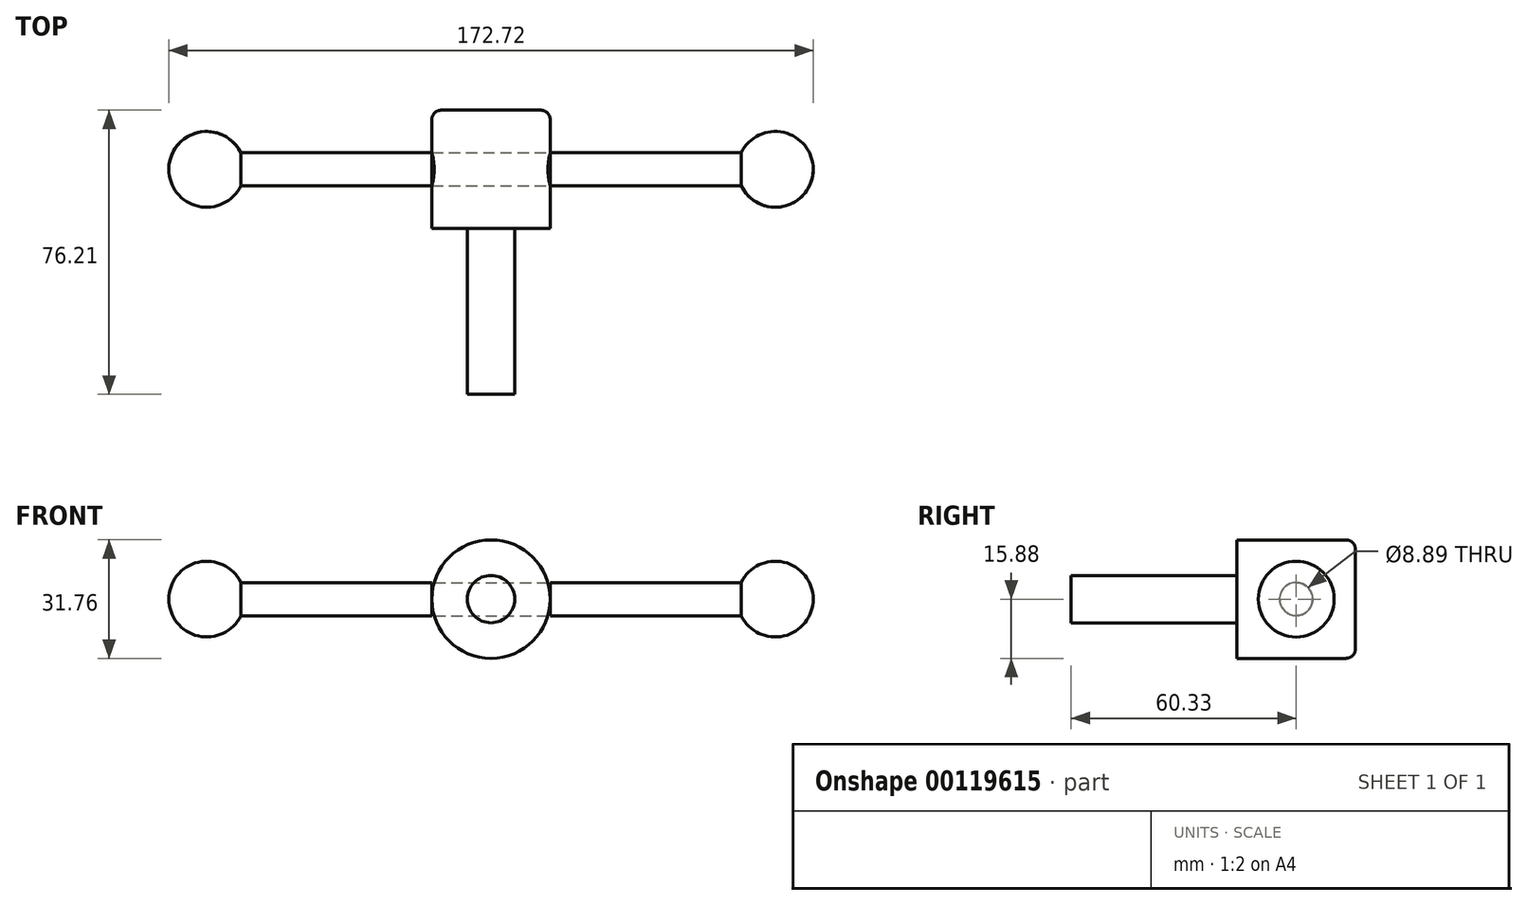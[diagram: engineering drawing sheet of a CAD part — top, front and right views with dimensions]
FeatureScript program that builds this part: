
annotation { "Feature Type Name" : "Feature", "Feature Type Description" : "" }
export const myFeature = defineFeature(function(context is Context, id is Id, definition is map)
    precondition{}
    {
        {
            var Q0;
            Q0=qCreatedBy(makeId("Top.planeOp"),FACE);
            var sketch = newSketch(context, id + "F0", { "sketchPlane" : qUnion([Q0])});
            skLineSegment(sketch, "E0", {"start": v(-76.2, 0) * mm, "end": v(76.2, 0) * mm, "construction": true});
            skLineSegment(sketch, "E1", {"start": v(0, 22.54) * mm, "end": v(0, -99.25) * mm, "construction": true});
            skLineSegment(sketch, "E2.bottom", {"start": v(-66.04, 0) * mm, "end": v(-15.87, 0) * mm});
            skLineSegment(sketch, "E2.top", {"start": v(-67.06, -4.45) * mm, "end": v(-15.87, -4.45) * mm});
            skLineSegment(sketch, "E2.right", {"start": v(-15.87, 0) * mm, "end": v(-15.87, -4.45) * mm});
            skLineSegment(sketch, "E3.bottom", {"start": v(-15.87, 15.87) * mm, "end": v(15.88, 15.87) * mm, "construction": true});
            skLineSegment(sketch, "E3.top", {"start": v(-15.87, -15.88) * mm, "end": v(15.88, -15.88) * mm, "construction": true});
            skLineSegment(sketch, "E3.left", {"start": v(-15.87, 15.87) * mm, "end": v(-15.87, -15.88) * mm});
            skLineSegment(sketch, "E3.right", {"start": v(15.88, 15.87) * mm, "end": v(15.88, -15.88) * mm, "construction": true});
            skLineSegment(sketch, "E4.bottom", {"start": v(66.04, 0) * mm, "end": v(15.88, 0) * mm});
            skLineSegment(sketch, "E4.top", {"start": v(67.06, -4.45) * mm, "end": v(15.88, -4.45) * mm});
            skLineSegment(sketch, "E4.right", {"start": v(15.88, 0) * mm, "end": v(15.88, -4.45) * mm});
            skArc(sketch, "E5", {"start": v(67.06, -4.44) * mm, "mid": v(78.48, -9.9) * mm, "end": v(86.36, 0) * mm});
            skArc(sketch, "E6", {"start": v(-86.36, 0) * mm, "mid": v(-78.48, -9.9) * mm, "end": v(-67.06, -4.45) * mm});
            skLineSegment(sketch, "E7.bottom", {"start": v(-6.35, -15.88) * mm, "end": v(0, -15.88) * mm});
            skLineSegment(sketch, "E7.top", {"start": v(-6.35, -60.33) * mm, "end": v(0, -60.33) * mm});
            skLineSegment(sketch, "E7.left", {"start": v(-6.35, -15.88) * mm, "end": v(-6.35, -60.33) * mm});
            skLineSegment(sketch, "E7.right", {"start": v(0, -15.88) * mm, "end": v(0, -60.33) * mm});
            skLineSegment(sketch, "E8", {"start": v(-66.04, 0) * mm, "end": v(-86.36, 0) * mm});
            skLineSegment(sketch, "E9", {"start": v(66.04, 0) * mm, "end": v(86.36, 0) * mm});
            skLineSegment(sketch, "E10", {"start": v(0, 15.87) * mm, "end": v(0, -15.88) * mm});
            skLineSegment(sketch, "E11", {"start": v(0, 15.87) * mm, "end": v(-15.87, 15.87) * mm});
            skLineSegment(sketch, "E12", {"start": v(0, -15.88) * mm, "end": v(-15.87, -15.88) * mm});
            skLineSegment(sketch, "E13", {"start": v(-15.87, 0) * mm, "end": v(15.88, 0) * mm});
            skLineSegment(sketch, "E14", {"start": v(-15.87, -4.45) * mm, "end": v(15.88, -4.44) * mm});
            skSolve(sketch);
        }
        {
            var Q0;
            {var subQ0=sQuery(id+"F0.wireOp",EDGE,"E10");Q0=makeQuery(id+"F0.imprint","IMPRINT",FACE,{"disambiguationData":[TD([[makeQuery(id+"F0.imprint","IMPRINT",EDGE,{"derivedFrom":subQ0}),-1.0]])]});}
            var Q1;
            Q1=makeQuery(id+"F0.imprint","IMPRINT",FACE,{"disambiguationData":[TD([[makeQuery(id+"F0.imprint","IMPRINT",EDGE,{"derivedFrom":sQuery(id+"F0.wireOp",EDGE,"E7.top")}),1.0]])]});
            var Q2;
            {var subQ0=sQuery(id+"F0.wireOp",EDGE,"E12");var subQ5=sQuery(id+"F0.wireOp",EDGE,"E3.left");var subQ6=makeQuery(id+"F0.imprint","INTERSECT",VERTEX,{"derivedFrom":[subQ5,subQ0]});Q2=makeQuery(id+"F0.imprint","IMPRINT",FACE,{"disambiguationData":[TD([[makeQuery(id+"F0.imprint","IMPRINT",EDGE,{"disambiguationData":[TD([[subQ6,1.0]])],"derivedFrom":subQ0}),-1.0]])]});}
            var Q3;
            Q3=sQuery(id+"F0.wireOp",EDGE,"E1");
            revolve(context, id + "F1", {"entities" : qUnion([Q0, Q1, Q2]), "axis" : qUnion([Q3]), "revolveType" : RevolveType.FULL});
        }
        {
            var Q0;
            Q0=qCreatedBy(makeId("Right.planeOp"),FACE);
            cPlane(context, id + "F2", {"entities" : qUnion([Q0]), "cplaneType" : CPlaneType.OFFSET, "offset" : 15.88 * mm, "width" : 152.4 * mm, "height" : 152.4 * mm});
        }
        {
            var Q0;
            Q0=qCreatedBy(id+"F2.planeOp",FACE);
            var sketch = newSketch(context, id + "F3", { "sketchPlane" : qUnion([Q0])});
            skCircle(sketch, "E15", {"center": v(0, 0) * mm, "radius": 4.45 * mm});
            skSolve(sketch);
        }
        {
            var Q0;
            Q0=makeQuery(id+"F3.imprint","IMPRINT",FACE,{"disambiguationData":[TD([[makeQuery(id+"F3.imprint","IMPRINT",EDGE,{"derivedFrom":sQuery(id+"F3.wireOp",EDGE,"E15")}),1.0]])]});
            extrude(context, id + "F4", {"entities" : qUnion([Q0]), "operationType" : NewBodyOperationType.REMOVE, "oppositeDirection" : true, "depth" : 31.75 * mm});
        }
        {
            var Q0;
            Q0=makeQuery(id+"F0.imprint","IMPRINT",FACE,{"disambiguationData":[TD([[makeQuery(id+"F0.imprint","IMPRINT",EDGE,{"derivedFrom":sQuery(id+"F0.wireOp",EDGE,"E4.bottom")}),1.0]])]});
            var Q1;
            {var subQ1=sQuery(id+"F0.wireOp",EDGE,"E2.bottom");Q1=makeQuery(id+"F0.imprint","IMPRINT",FACE,{"disambiguationData":[TD([[makeQuery(id+"F0.imprint","IMPRINT",EDGE,{"derivedFrom":subQ1}),-1.0]])]});}
            var Q2;
            Q2=sQuery(id+"F0.wireOp",EDGE,"E4.bottom");
            revolve(context, id + "F5", {"entities" : qUnion([Q0, Q1]), "axis" : qUnion([Q2]), "revolveType" : RevolveType.FULL});
        }
        {
            var Q0;
            Q0=makeQuery(id+"F1.opRevolve","SWEPT_EDGE",EDGE,{"disambiguationData":[OSD([sQuery(id+"F0.wireOp",EDGE,"E3.left"),sQuery(id+"F0.wireOp",EDGE,"E11")])]});
            fillet(context, id + "F6", {"entities" : qUnion([Q0]), "radius" : 2.54 * mm, "tangentPropagation" : true, "allowEdgeOverflow" : false});
        }
    });
